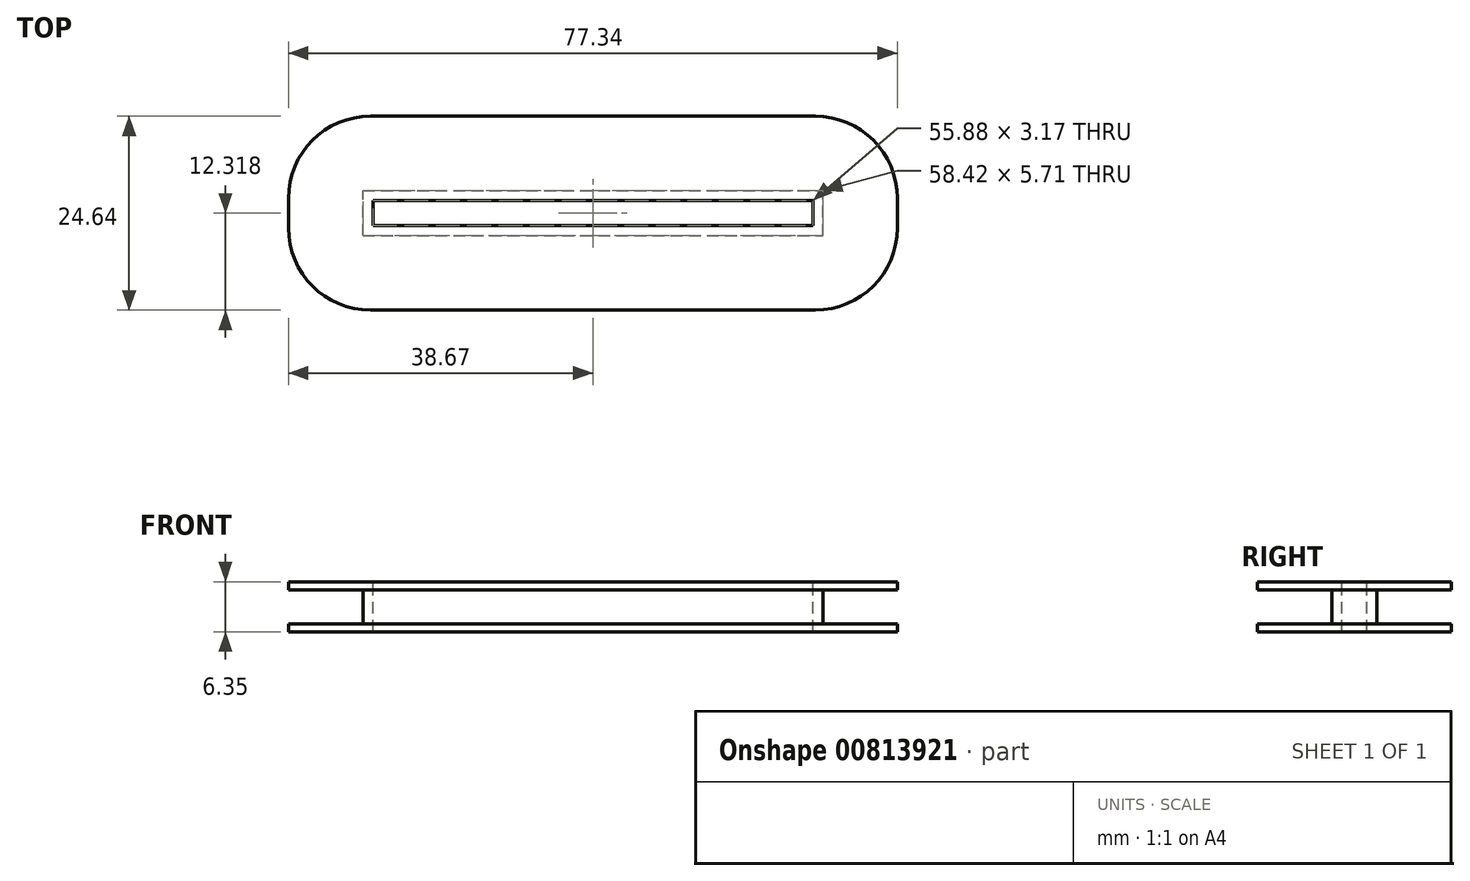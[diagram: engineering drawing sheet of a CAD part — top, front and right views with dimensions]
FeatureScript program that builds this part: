
annotation { "Feature Type Name" : "Feature", "Feature Type Description" : "" }
export const myFeature = defineFeature(function(context is Context, id is Id, definition is map)
    precondition{}
    {
        {
            var Q0;
            Q0=qCreatedBy(makeId("Top.planeOp"),FACE);
            var sketch = newSketch(context, id + "F0", { "sketchPlane" : qUnion([Q0])});
            skLineSegment(sketch, "E0.bottom", {"start": v(0, 0) * mm, "end": v(55.88, 0) * mm});
            skLineSegment(sketch, "E0.top", {"start": v(0, 3.18) * mm, "end": v(55.88, 3.18) * mm});
            skLineSegment(sketch, "E0.left", {"start": v(0, 0) * mm, "end": v(0, 3.18) * mm});
            skLineSegment(sketch, "E0.right", {"start": v(55.88, 0) * mm, "end": v(55.88, 3.18) * mm});
            skPoint(sketch, "E1.firstSnap0", {"position": v(0, 1.59) * mm});
            skPoint(sketch, "E1.oppositeSnap0", {"position": v(0, 1.59) * mm});
            skLineSegment(sketch, "E1.bottom", {"start": v(-1.4, 1.59) * mm, "end": v(-2.3, 1.59) * mm});
            skLineSegment(sketch, "E1.top", {"start": v(-1.4, 1.59) * mm, "end": v(-2.3, 1.59) * mm});
            skLineSegment(sketch, "E1.left", {"start": v(-1.4, 1.59) * mm, "end": v(-1.4, 1.59) * mm});
            skLineSegment(sketch, "E1.right", {"start": v(-2.3, 1.59) * mm, "end": v(-2.3, 1.59) * mm});
            skLineSegment(sketch, "E2.0", {"start": v(-1.27, 4.45) * mm, "end": v(57.15, 4.45) * mm});
            skLineSegment(sketch, "E2.1", {"start": v(-1.27, -1.27) * mm, "end": v(-1.27, 4.45) * mm});
            skLineSegment(sketch, "E2.2", {"start": v(-1.27, -1.27) * mm, "end": v(57.15, -1.27) * mm});
            skLineSegment(sketch, "E2.3", {"start": v(57.15, -1.27) * mm, "end": v(57.15, 4.45) * mm});
            skLineSegment(sketch, "E3.0", {"start": v(-0.32, 13.9) * mm, "end": v(56.2, 13.9) * mm});
            skLineSegment(sketch, "E3.1", {"start": v(-10.73, -0.32) * mm, "end": v(-10.73, 3.5) * mm});
            skLineSegment(sketch, "E3.2", {"start": v(-0.32, -10.73) * mm, "end": v(56.2, -10.73) * mm});
            skLineSegment(sketch, "E3.3", {"start": v(66.61, -0.32) * mm, "end": v(66.61, 3.5) * mm});
            skPoint(sketch, "E4.visualSharp", {"position": v(-10.73, 13.9) * mm});
            skArc(sketch, "E4.filletArc", {"start": v(-0.32, 13.9) * mm, "mid": v(-7.68, 10.86) * mm, "end": v(-10.73, 3.5) * mm});
            skPoint(sketch, "E5.visualSharp", {"position": v(-10.73, -10.73) * mm});
            skArc(sketch, "E5.filletArc", {"start": v(-10.73, -0.32) * mm, "mid": v(-7.68, -7.68) * mm, "end": v(-0.32, -10.73) * mm});
            skPoint(sketch, "E6.visualSharp", {"position": v(66.61, 13.9) * mm});
            skArc(sketch, "E6.filletArc", {"start": v(66.61, 3.5) * mm, "mid": v(63.56, 10.86) * mm, "end": v(56.2, 13.9) * mm});
            skPoint(sketch, "E7.visualSharp", {"position": v(66.61, -10.73) * mm});
            skArc(sketch, "E7.filletArc", {"start": v(56.2, -10.73) * mm, "mid": v(63.56, -7.68) * mm, "end": v(66.61, -0.32) * mm});
            skSolve(sketch);
        }
        {
            var Q0;
            Q0=makeQuery(id+"F0.imprint","IMPRINT",FACE,{"disambiguationData":[TD([[makeQuery(id+"F0.imprint","IMPRINT",EDGE,{"derivedFrom":sQuery(id+"F0.wireOp",EDGE,"E2.0")}),1.0]])]});
            var Q1;
            Q1=makeQuery(id+"F0.imprint","IMPRINT",FACE,{"disambiguationData":[TD([[makeQuery(id+"F0.imprint","IMPRINT",EDGE,{"derivedFrom":sQuery(id+"F0.wireOp",EDGE,"E0.bottom")}),-1.0]])]});
            extrude(context, id + "F1", {"entities" : qUnion([Q0, Q1]), "oppositeDirection" : true, "depth" : 6.35 * mm, "offsetDistance" : 25.4 * mm});
        }
        {
            var Q0;
            Q0=makeQuery(id+"F0.imprint","IMPRINT",FACE,{"disambiguationData":[TD([[makeQuery(id+"F0.imprint","IMPRINT",EDGE,{"derivedFrom":sQuery(id+"F0.wireOp",EDGE,"E2.0")}),1.0]])]});
            extrude(context, id + "F2", {"entities" : qUnion([Q0]), "operationType" : NewBodyOperationType.REMOVE, "oppositeDirection" : true, "depth" : 5.33 * mm, "offsetDistance" : 25.4 * mm});
        }
        {
            var Q0;
            Q0=makeQuery(id+"F0.imprint","IMPRINT",FACE,{"disambiguationData":[TD([[makeQuery(id+"F0.imprint","IMPRINT",EDGE,{"derivedFrom":sQuery(id+"F0.wireOp",EDGE,"E2.0")}),1.0]])]});
            extrude(context, id + "F3", {"entities" : qUnion([Q0]), "operationType" : NewBodyOperationType.ADD, "oppositeDirection" : true, "depth" : 1.02 * mm, "offsetDistance" : 25.4 * mm});
        }
    });
